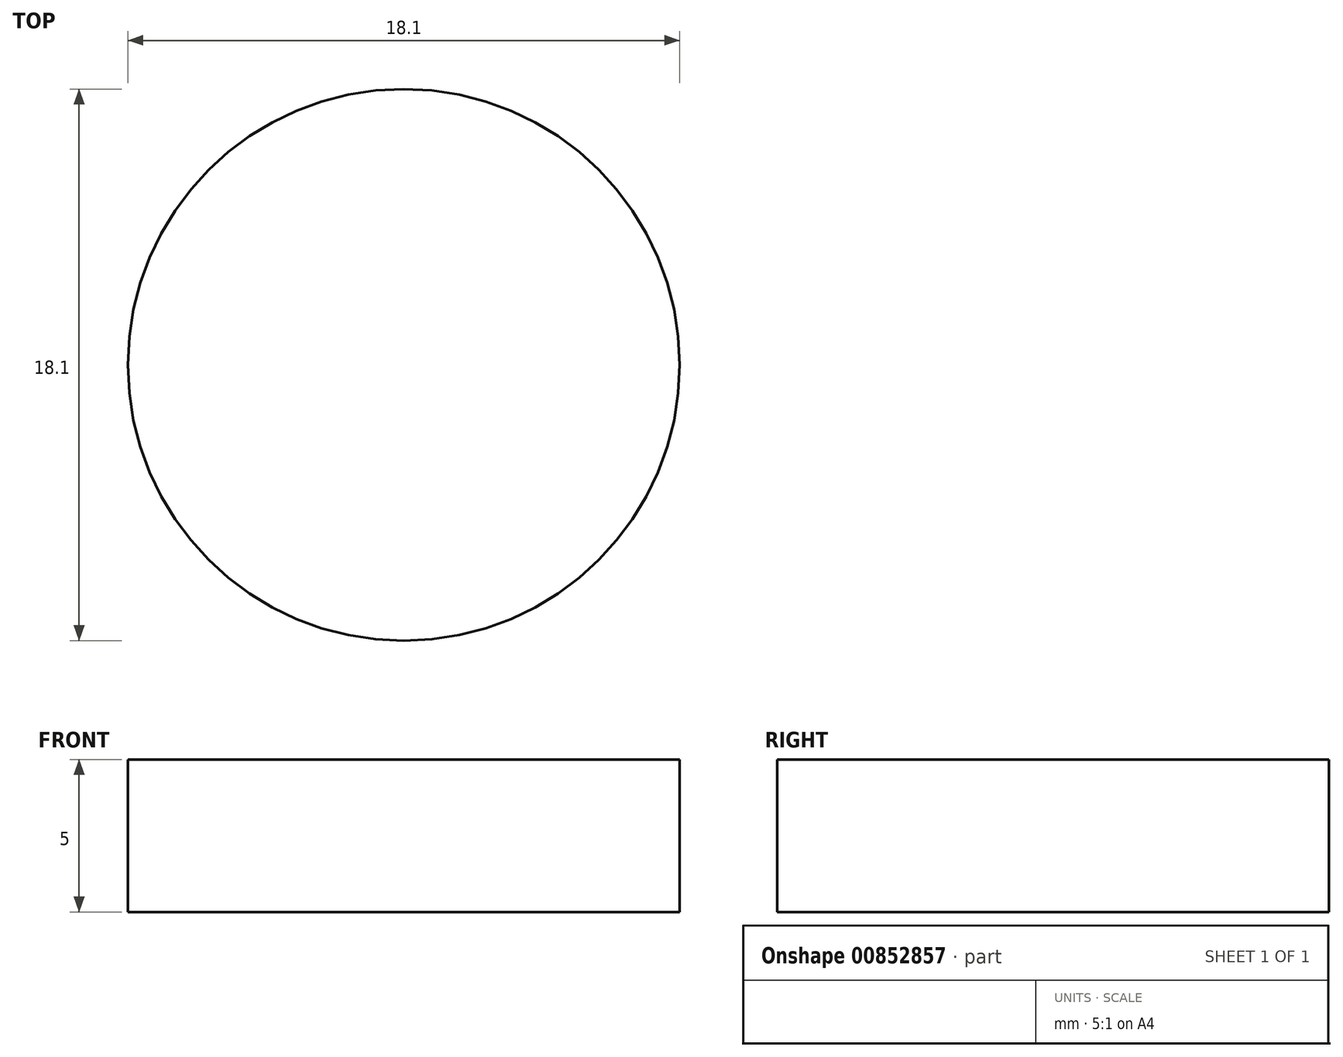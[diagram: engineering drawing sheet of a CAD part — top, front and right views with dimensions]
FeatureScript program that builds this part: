
annotation { "Feature Type Name" : "Feature", "Feature Type Description" : "" }
export const myFeature = defineFeature(function(context is Context, id is Id, definition is map)
    precondition{}
    {
        {
            var Q0;
            Q0=qCreatedBy(makeId("Top.planeOp"),FACE);
            var sketch = newSketch(context, id + "F0", { "sketchPlane" : qUnion([Q0])});
            skCircle(sketch, "E0", {"center": v(0, 0) * mm, "radius": 9.05 * mm});
            skSolve(sketch);
        }
        {
            var Q0;
            Q0=makeQuery(id+"F0.imprint","IMPRINT",FACE,{"disambiguationData":[TD([[makeQuery(id+"F0.imprint","IMPRINT",EDGE,{"derivedFrom":sQuery(id+"F0.wireOp",EDGE,"E0")}),1.0]])]});
            extrude(context, id + "F1", {"entities" : qUnion([Q0]), "depth" : 5 * mm, "offsetDistance" : 25 * mm});
        }
    });
